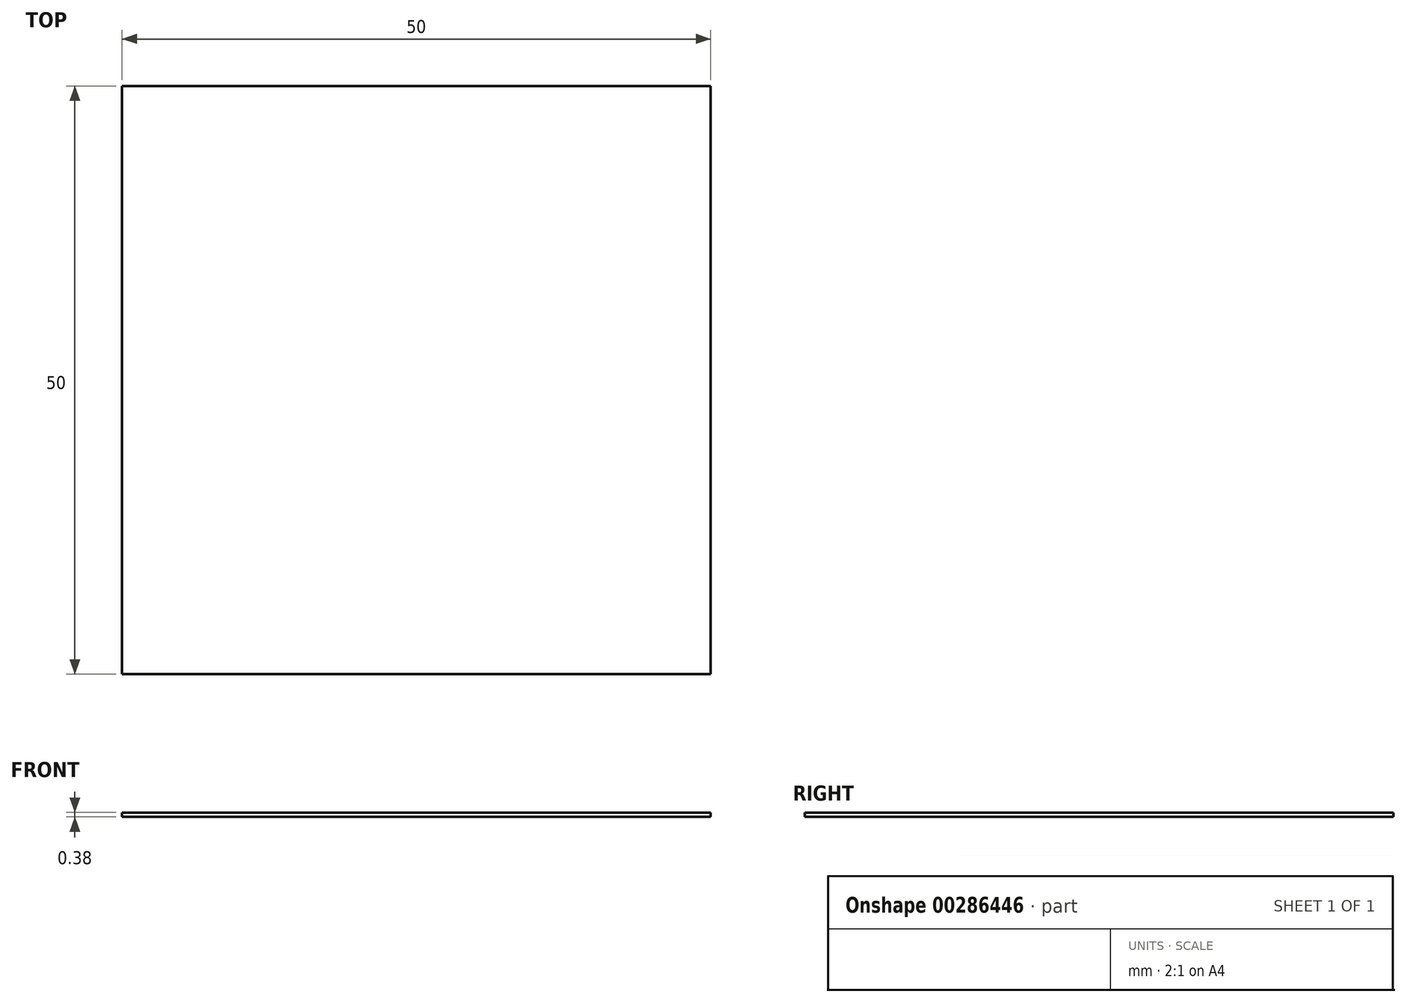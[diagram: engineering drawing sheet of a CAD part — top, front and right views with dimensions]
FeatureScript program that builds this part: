
annotation { "Feature Type Name" : "Feature", "Feature Type Description" : "" }
export const myFeature = defineFeature(function(context is Context, id is Id, definition is map)
    precondition{}
    {
        {
            var Q0;
            Q0=qCreatedBy(makeId("Top.planeOp"),FACE);
            var sketch = newSketch(context, id + "F0", { "sketchPlane" : qUnion([Q0])});
            skLineSegment(sketch, "E0.bottom", {"start": v(0, 0) * mm, "end": v(50, 0) * mm});
            skLineSegment(sketch, "E0.top", {"start": v(0, -50) * mm, "end": v(50, -50) * mm});
            skLineSegment(sketch, "E0.left", {"start": v(0, 0) * mm, "end": v(0, -50) * mm});
            skLineSegment(sketch, "E0.right", {"start": v(50, 0) * mm, "end": v(50, -50) * mm});
            skSolve(sketch);
        }
        {
            var Q0;
            Q0=makeQuery(id+"F0.imprint","IMPRINT",FACE,{"disambiguationData":[TD([[makeQuery(id+"F0.imprint","IMPRINT",EDGE,{"derivedFrom":sQuery(id+"F0.wireOp",EDGE,"E0.bottom")}),-1.0]])]});
            extrude(context, id + "F1", {"entities" : qUnion([Q0]), "depth" : 0.38 * mm});
        }
    });
